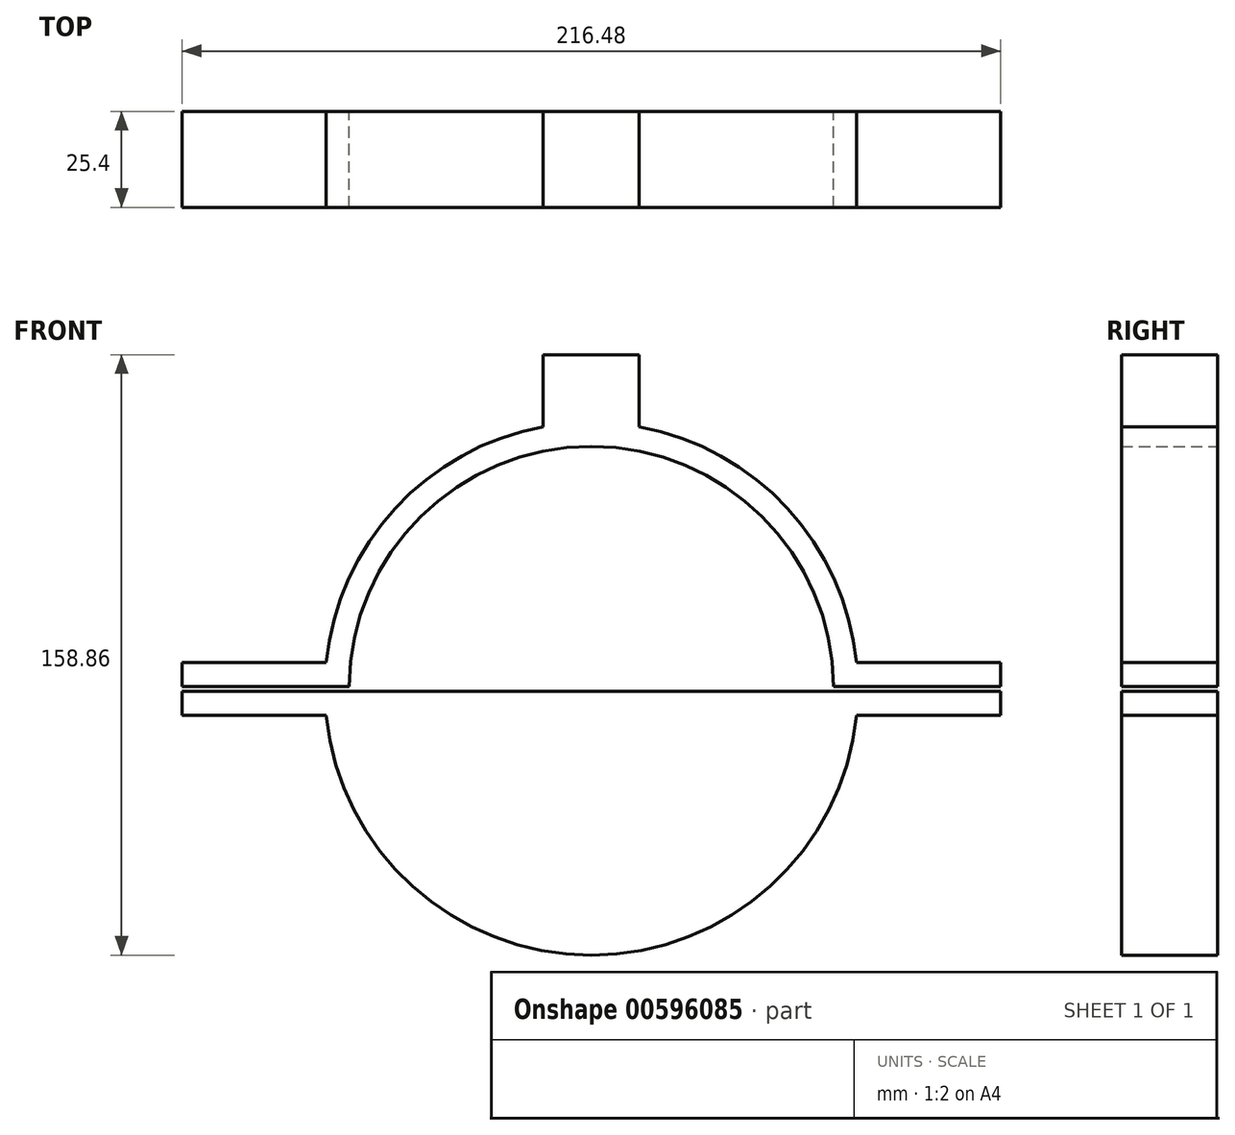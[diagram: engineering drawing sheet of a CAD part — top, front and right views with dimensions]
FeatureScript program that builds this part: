
annotation { "Feature Type Name" : "Feature", "Feature Type Description" : "" }
export const myFeature = defineFeature(function(context is Context, id is Id, definition is map)
    precondition{}
    {
        {
            var Q0;
            Q0=qCreatedBy(makeId("Front.planeOp"),FACE);
            var sketch = newSketch(context, id + "F0", { "sketchPlane" : qUnion([Q0])});
            skArc(sketch, "E0", {"start": v(-64.13, -0.64) * mm, "mid": v(0, -64.13) * mm, "end": v(64.13, -0.63) * mm});
            skArc(sketch, "E1", {"start": v(-12.7, 69.33) * mm, "mid": v(-51.84, 47.76) * mm, "end": v(-70.14, 6.98) * mm});
            skLineSegment(sketch, "E2", {"start": v(-12.7, 69.33) * mm, "end": v(-12.7, 88.38) * mm});
            skLineSegment(sketch, "E3", {"start": v(-12.7, 88.38) * mm, "end": v(12.7, 88.38) * mm});
            skLineSegment(sketch, "E4", {"start": v(12.7, 88.38) * mm, "end": v(12.7, 69.33) * mm});
            skLineSegment(sketch, "E5", {"start": v(0, -70.48) * mm, "end": v(0, 88.38) * mm, "construction": true});
            skLineSegment(sketch, "E6", {"start": v(-108.24, 0) * mm, "end": v(64.13, 0) * mm, "construction": true});
            skLineSegment(sketch, "E7", {"start": v(-108.24, 0.64) * mm, "end": v(-64.13, 0.64) * mm});
            skLineSegment(sketch, "E8", {"start": v(-108.24, 0.64) * mm, "end": v(-108.24, 6.99) * mm});
            skLineSegment(sketch, "E9", {"start": v(-108.24, 6.99) * mm, "end": v(-70.14, 6.99) * mm});
            skLineSegment(sketch, "E10.MirrorCS", {"start": v(-108.24, -0.64) * mm, "end": v(0, -0.64) * mm});
            skLineSegment(sketch, "E11.MirrorCS", {"start": v(-108.24, -0.64) * mm, "end": v(-108.24, -6.99) * mm});
            skLineSegment(sketch, "E12.MirrorCS", {"start": v(-108.24, -6.99) * mm, "end": v(-70.14, -6.99) * mm});
            skLineSegment(sketch, "E13.trimOffspring", {"start": v(64.13, 0.64) * mm, "end": v(70.48, 0.64) * mm});
            skArc(sketch, "E14.trimOffspring", {"start": v(-70.14, -6.99) * mm, "mid": v(0, -70.48) * mm, "end": v(70.14, -6.99) * mm});
            skLineSegment(sketch, "E15.trimOffspring", {"start": v(64.13, -0.64) * mm, "end": v(70.48, -0.64) * mm});
            skLineSegment(sketch, "E16.MirrorCS", {"start": v(108.24, -6.99) * mm, "end": v(70.14, -6.99) * mm});
            skLineSegment(sketch, "E17.MirrorCS", {"start": v(108.24, -0.64) * mm, "end": v(108.24, -6.99) * mm});
            skLineSegment(sketch, "E18.MirrorCS", {"start": v(108.24, -0.64) * mm, "end": v(0, -0.64) * mm});
            skLineSegment(sketch, "E19.MirrorCS", {"start": v(108.24, 0.64) * mm, "end": v(64.13, 0.64) * mm});
            skLineSegment(sketch, "E20.MirrorCS", {"start": v(108.24, 0.64) * mm, "end": v(108.24, 6.99) * mm});
            skLineSegment(sketch, "E21.MirrorCS", {"start": v(108.24, 6.99) * mm, "end": v(70.14, 6.99) * mm});
            skArc(sketch, "E22.trimOffspring", {"start": v(64.13, 0.64) * mm, "mid": v(0, 64.13) * mm, "end": v(-64.13, 0.64) * mm});
            skArc(sketch, "E23.trimOffspring", {"start": v(70.14, 6.99) * mm, "mid": v(51.84, 47.76) * mm, "end": v(12.7, 69.33) * mm});
            skSolve(sketch);
        }
        {
            var Q0;
            Q0 = qSketchRegion(id + "F0", true);
            extrude(context, id + "F1", {"entities" : qUnion([Q0]), "depth" : 25.4 * mm, "offsetDistance" : 25.4 * mm});
        }
    });
